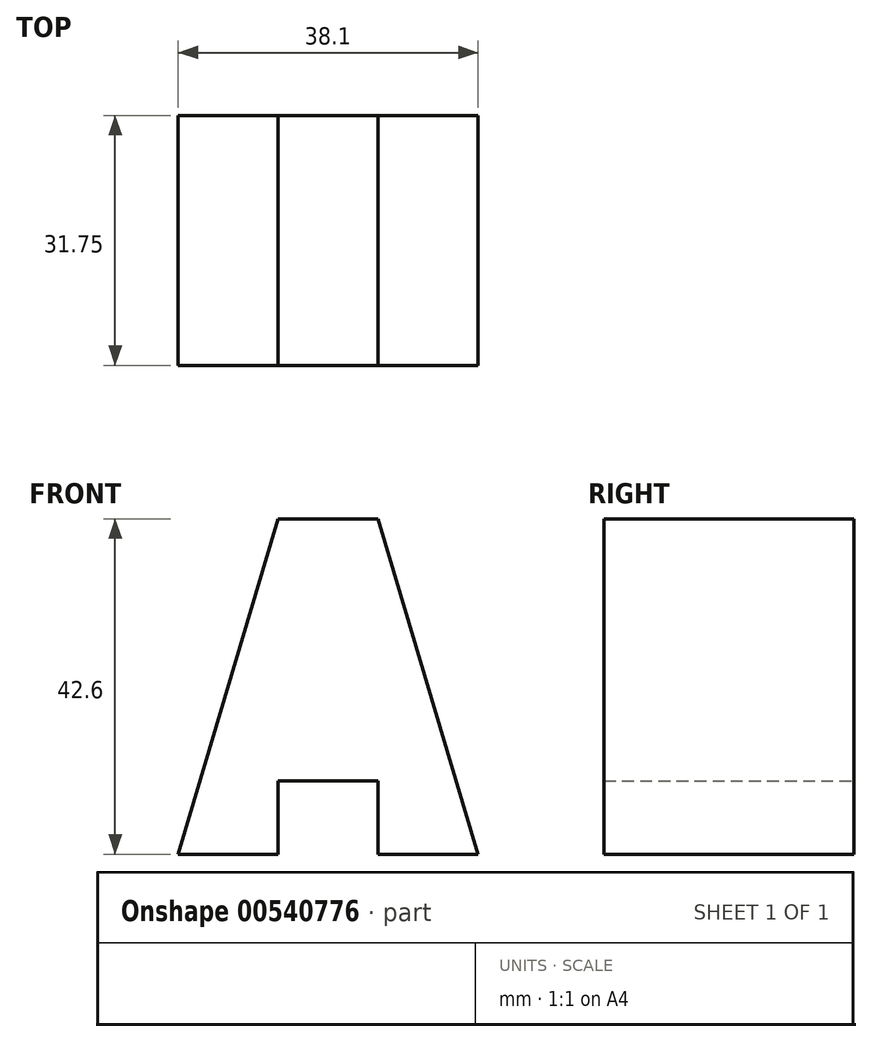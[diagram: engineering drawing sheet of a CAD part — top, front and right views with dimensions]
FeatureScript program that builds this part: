
annotation { "Feature Type Name" : "Feature", "Feature Type Description" : "" }
export const myFeature = defineFeature(function(context is Context, id is Id, definition is map)
    precondition{}
    {
        {
            var Q0;
            Q0=qCreatedBy(makeId("Front.planeOp"),FACE);
            var sketch = newSketch(context, id + "F0", { "sketchPlane" : qUnion([Q0])});
            skLineSegment(sketch, "E0", {"start": v(7.13, 0) * mm, "end": v(19.83, 42.6) * mm});
            skLineSegment(sketch, "E1", {"start": v(19.83, 42.6) * mm, "end": v(32.53, 42.6) * mm});
            skLineSegment(sketch, "E2", {"start": v(32.53, 42.6) * mm, "end": v(45.23, 0) * mm});
            skLineSegment(sketch, "E3", {"start": v(45.23, 0) * mm, "end": v(32.53, 0) * mm});
            skLineSegment(sketch, "E4", {"start": v(32.53, 0) * mm, "end": v(32.53, 9.3) * mm});
            skLineSegment(sketch, "E5", {"start": v(32.53, 9.3) * mm, "end": v(19.83, 9.3) * mm});
            skLineSegment(sketch, "E6", {"start": v(19.83, 9.3) * mm, "end": v(19.83, 0) * mm});
            skLineSegment(sketch, "E7", {"start": v(19.83, 0) * mm, "end": v(7.13, 0) * mm});
            skSolve(sketch);
        }
        {
            var Q0;
            Q0 = qSketchRegion(id + "F0", true);
            extrude(context, id + "F1", {"entities" : qUnion([Q0]), "depth" : 31.75 * mm, "offsetDistance" : 25.4 * mm});
        }
    });
